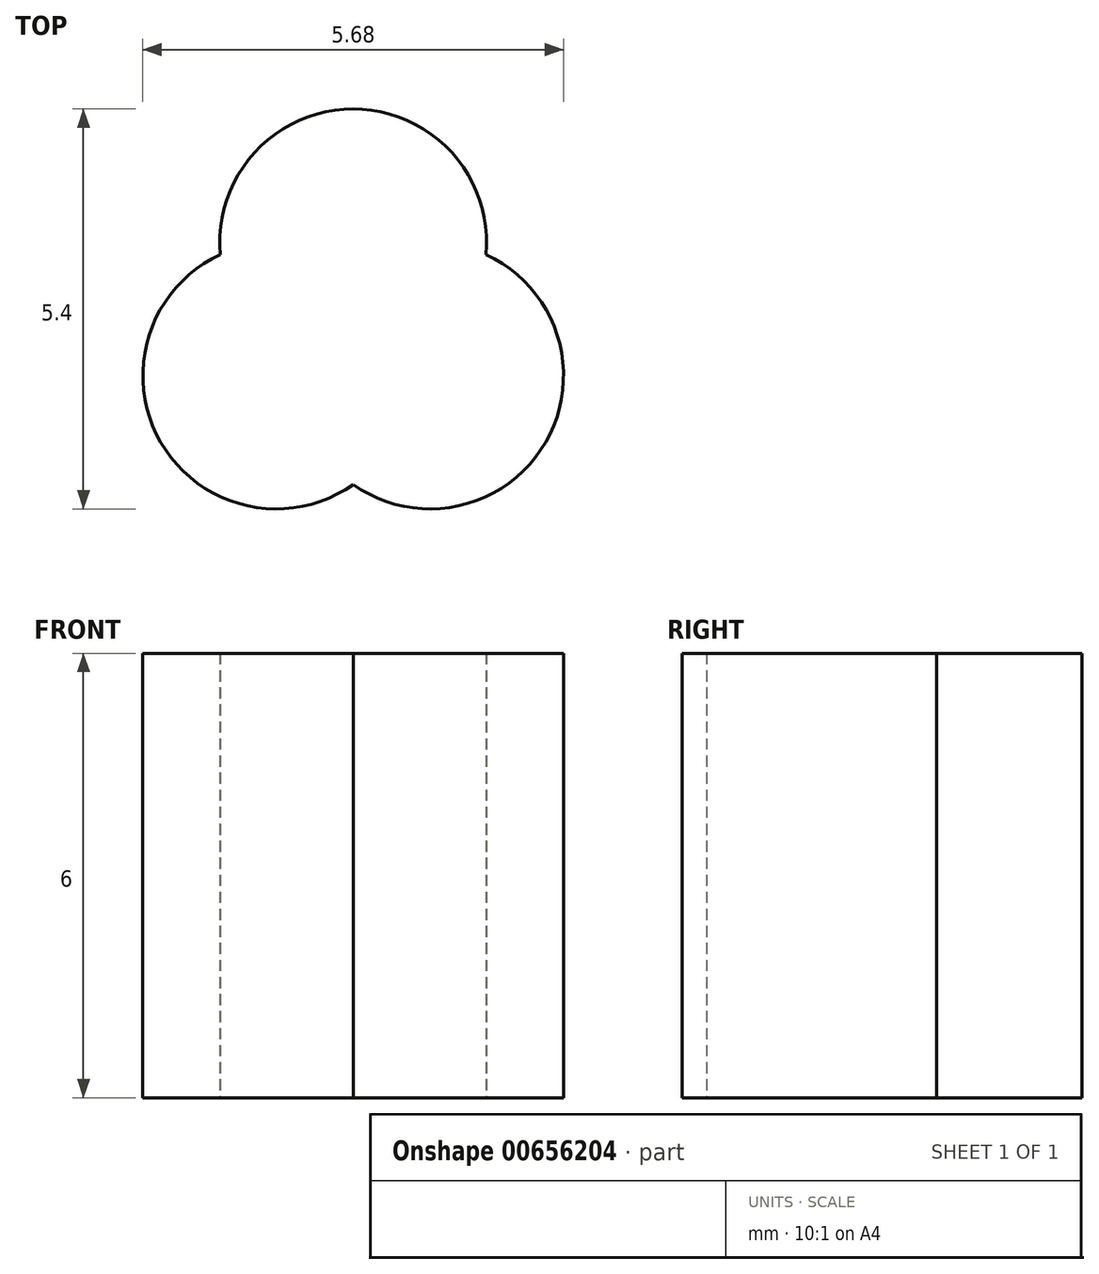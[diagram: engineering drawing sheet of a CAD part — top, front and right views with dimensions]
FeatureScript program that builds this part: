
annotation { "Feature Type Name" : "Feature", "Feature Type Description" : "" }
export const myFeature = defineFeature(function(context is Context, id is Id, definition is map)
    precondition{}
    {
        {
            var Q0;
            Q0=qCreatedBy(makeId("Top.planeOp"),FACE);
            var sketch = newSketch(context, id + "F0", { "sketchPlane" : qUnion([Q0])});
            skCircle(sketch, "E0", {"center": v(0, 0) * mm, "radius": 3 * mm});
            skCircle(sketch, "E1", {"center": v(0, 1.2) * mm, "radius": 1.8 * mm});
            skCircle(sketch, "E2", {"center": v(1.04, -0.6) * mm, "radius": 1.8 * mm});
            skCircle(sketch, "E3", {"center": v(-1.04, -0.6) * mm, "radius": 1.8 * mm});
            skLineSegment(sketch, "E4", {"start": v(0, 1.2) * mm, "end": v(1.04, -0.6) * mm});
            skLineSegment(sketch, "E5", {"start": v(0, 1.2) * mm, "end": v(-1.04, -0.6) * mm});
            skLineSegment(sketch, "E6", {"start": v(-1.04, -0.6) * mm, "end": v(1.04, -0.6) * mm});
            skSolve(sketch);
        }
        {
            var Q0;
            {var subQ1=sQuery(id+"F0.wireOp",EDGE,"E1");var subQ5=makeQuery(id+"F0.imprint","INTERSECT",VERTEX,{"derivedFrom":[sQuery(id+"F0.wireOp",EDGE,"E0"),subQ1]});Q0=makeQuery(id+"F0.imprint","IMPRINT",FACE,{"disambiguationData":[TD([[makeQuery(id+"F0.imprint","IMPRINT",EDGE,{"disambiguationData":[TD([[subQ5,-1.0]])],"derivedFrom":subQ1}),1.0]])]});}
            var Q1;
            {var subQ0=sQuery(id+"F0.wireOp",EDGE,"E4");var subQ1=sQuery(id+"F0.wireOp",EDGE,"E2");var subQ2=makeQuery(id+"F0.imprint","INTERSECT",VERTEX,{"derivedFrom":[subQ1,subQ0]});Q1=makeQuery(id+"F0.imprint","IMPRINT",FACE,{"disambiguationData":[TD([[makeQuery(id+"F0.imprint","IMPRINT",EDGE,{"disambiguationData":[TD([[subQ2,-1.0]])],"derivedFrom":subQ1}),-1.0]])]});}
            var Q2;
            {var subQ0=sQuery(id+"F0.wireOp",EDGE,"E4");var subQ1=sQuery(id+"F0.wireOp",EDGE,"E2");var subQ2=makeQuery(id+"F0.imprint","INTERSECT",VERTEX,{"derivedFrom":[subQ1,subQ0]});Q2=makeQuery(id+"F0.imprint","IMPRINT",FACE,{"disambiguationData":[TD([[makeQuery(id+"F0.imprint","IMPRINT",EDGE,{"disambiguationData":[TD([[subQ2,-1.0]])],"derivedFrom":subQ1}),1.0]])]});}
            var Q3;
            {var subQ0=sQuery(id+"F0.wireOp",EDGE,"E2");var subQ1=sQuery(id+"F0.wireOp",EDGE,"E1");var subQ2=makeQuery(id+"F0.imprint","INTERSECT",VERTEX,{"disambiguationData":[OD(0.0)],"derivedFrom":[subQ1,subQ0]});Q3=makeQuery(id+"F0.imprint","IMPRINT",FACE,{"disambiguationData":[TD([[makeQuery(id+"F0.imprint","IMPRINT",EDGE,{"disambiguationData":[TD([[subQ2,-1.0]])],"derivedFrom":subQ1}),1.0]])]});}
            var Q4;
            {var subQ0=sQuery(id+"F0.wireOp",EDGE,"E3");var subQ1=sQuery(id+"F0.wireOp",EDGE,"E2");var subQ2=makeQuery(id+"F0.imprint","INTERSECT",VERTEX,{"disambiguationData":[OD(0.0)],"derivedFrom":[subQ1,subQ0]});Q4=makeQuery(id+"F0.imprint","IMPRINT",FACE,{"disambiguationData":[TD([[makeQuery(id+"F0.imprint","IMPRINT",EDGE,{"disambiguationData":[TD([[subQ2,-1.0]])],"derivedFrom":subQ1}),-1.0]])]});}
            var Q5;
            {var subQ0=sQuery(id+"F0.wireOp",EDGE,"E3");var subQ1=sQuery(id+"F0.wireOp",EDGE,"E1");var subQ2=makeQuery(id+"F0.imprint","INTERSECT",VERTEX,{"disambiguationData":[OD(0.0)],"derivedFrom":[subQ1,subQ0]});Q5=makeQuery(id+"F0.imprint","IMPRINT",FACE,{"disambiguationData":[TD([[makeQuery(id+"F0.imprint","IMPRINT",EDGE,{"disambiguationData":[TD([[subQ2,-1.0]])],"derivedFrom":subQ1}),1.0]])]});}
            var Q6;
            {var subQ0=sQuery(id+"F0.wireOp",EDGE,"E4");var subQ1=sQuery(id+"F0.wireOp",EDGE,"E1");var subQ2=makeQuery(id+"F0.imprint","INTERSECT",VERTEX,{"derivedFrom":[subQ1,subQ0]});Q6=makeQuery(id+"F0.imprint","IMPRINT",FACE,{"disambiguationData":[TD([[makeQuery(id+"F0.imprint","IMPRINT",EDGE,{"disambiguationData":[TD([[subQ2,-1.0]])],"derivedFrom":subQ1}),1.0]])]});}
            var Q7;
            {var subQ6=sQuery(id+"F0.wireOp",EDGE,"E1");var subQ8=sQuery(id+"F0.wireOp",EDGE,"E4");var subQ9=makeQuery(id+"F0.imprint","INTERSECT",VERTEX,{"derivedFrom":[subQ6,subQ8]});Q7=makeQuery(id+"F0.imprint","IMPRINT",FACE,{"disambiguationData":[TD([[makeQuery(id+"F0.imprint","IMPRINT",EDGE,{"disambiguationData":[TD([[subQ9,-1.0]])],"derivedFrom":subQ6}),-1.0]])]});}
            var Q8;
            {var subQ0=sQuery(id+"F0.wireOp",EDGE,"E3");var subQ1=sQuery(id+"F0.wireOp",EDGE,"E1");var subQ2=makeQuery(id+"F0.imprint","INTERSECT",VERTEX,{"disambiguationData":[OD(1.0)],"derivedFrom":[subQ1,subQ0]});Q8=makeQuery(id+"F0.imprint","IMPRINT",FACE,{"disambiguationData":[TD([[makeQuery(id+"F0.imprint","IMPRINT",EDGE,{"disambiguationData":[TD([[subQ2,-1.0]])],"derivedFrom":subQ1}),1.0]])]});}
            var Q9;
            {var subQ0=sQuery(id+"F0.wireOp",EDGE,"E3");var subQ1=sQuery(id+"F0.wireOp",EDGE,"E1");var subQ2=makeQuery(id+"F0.imprint","INTERSECT",VERTEX,{"disambiguationData":[OD(1.0)],"derivedFrom":[subQ1,subQ0]});Q9=makeQuery(id+"F0.imprint","IMPRINT",FACE,{"disambiguationData":[TD([[makeQuery(id+"F0.imprint","IMPRINT",EDGE,{"disambiguationData":[TD([[subQ2,-1.0]])],"derivedFrom":subQ1}),-1.0]])]});}
            var Q10;
            {var subQ0=sQuery(id+"F0.wireOp",EDGE,"E6");var subQ1=sQuery(id+"F0.wireOp",EDGE,"E1");var subQ2=makeQuery(id+"F0.imprint","INTERSECT",VERTEX,{"derivedFrom":[subQ1,subQ0]});Q10=makeQuery(id+"F0.imprint","IMPRINT",FACE,{"disambiguationData":[TD([[makeQuery(id+"F0.imprint","IMPRINT",EDGE,{"disambiguationData":[TD([[subQ2,-1.0]])],"derivedFrom":subQ1}),-1.0]])]});}
            var Q11;
            {var subQ0=sQuery(id+"F0.wireOp",EDGE,"E2");var subQ1=sQuery(id+"F0.wireOp",EDGE,"E1");var subQ2=makeQuery(id+"F0.imprint","INTERSECT",VERTEX,{"disambiguationData":[OD(0.0)],"derivedFrom":[subQ1,subQ0]});Q11=makeQuery(id+"F0.imprint","IMPRINT",FACE,{"disambiguationData":[TD([[makeQuery(id+"F0.imprint","IMPRINT",EDGE,{"disambiguationData":[TD([[subQ2,-1.0]])],"derivedFrom":subQ1}),-1.0]])]});}
            var Q12;
            {var subQ0=sQuery(id+"F0.wireOp",EDGE,"E5");var subQ1=sQuery(id+"F0.wireOp",EDGE,"E1");var subQ2=makeQuery(id+"F0.imprint","INTERSECT",VERTEX,{"derivedFrom":[subQ1,subQ0]});Q12=makeQuery(id+"F0.imprint","IMPRINT",FACE,{"disambiguationData":[TD([[makeQuery(id+"F0.imprint","IMPRINT",EDGE,{"disambiguationData":[TD([[subQ2,-1.0]])],"derivedFrom":subQ1}),-1.0]])]});}
            var Q13;
            {var subQ0=sQuery(id+"F0.wireOp",EDGE,"E5");var subQ1=sQuery(id+"F0.wireOp",EDGE,"E1");var subQ2=makeQuery(id+"F0.imprint","INTERSECT",VERTEX,{"derivedFrom":[subQ1,subQ0]});Q13=makeQuery(id+"F0.imprint","IMPRINT",FACE,{"disambiguationData":[TD([[makeQuery(id+"F0.imprint","IMPRINT",EDGE,{"disambiguationData":[TD([[subQ2,-1.0]])],"derivedFrom":subQ1}),1.0]])]});}
            var Q14;
            {var subQ0=sQuery(id+"F0.wireOp",EDGE,"E6");var subQ1=sQuery(id+"F0.wireOp",EDGE,"E2");var subQ2=makeQuery(id+"F0.imprint","INTERSECT",VERTEX,{"derivedFrom":[subQ1,subQ0]});Q14=makeQuery(id+"F0.imprint","IMPRINT",FACE,{"disambiguationData":[TD([[makeQuery(id+"F0.imprint","IMPRINT",EDGE,{"disambiguationData":[TD([[subQ2,-1.0]])],"derivedFrom":subQ1}),1.0]])]});}
            var Q15;
            {var subQ0=sQuery(id+"F0.wireOp",EDGE,"E3");var subQ6=sQuery(id+"F0.wireOp",EDGE,"E1");var subQ7=makeQuery(id+"F0.imprint","INTERSECT",VERTEX,{"disambiguationData":[OD(0.0)],"derivedFrom":[subQ6,subQ0]});Q15=makeQuery(id+"F0.imprint","IMPRINT",FACE,{"disambiguationData":[TD([[makeQuery(id+"F0.imprint","IMPRINT",EDGE,{"disambiguationData":[TD([[subQ7,-1.0]])],"derivedFrom":subQ6}),-1.0]])]});}
            extrude(context, id + "F1", {"entities" : qUnion([Q0, Q1, Q2, Q3, Q4, Q5, Q6, Q7, Q8, Q9, Q10, Q11, Q12, Q13, Q14, Q15]), "depth" : 6 * mm, "offsetDistance" : 25 * mm});
        }
    });
